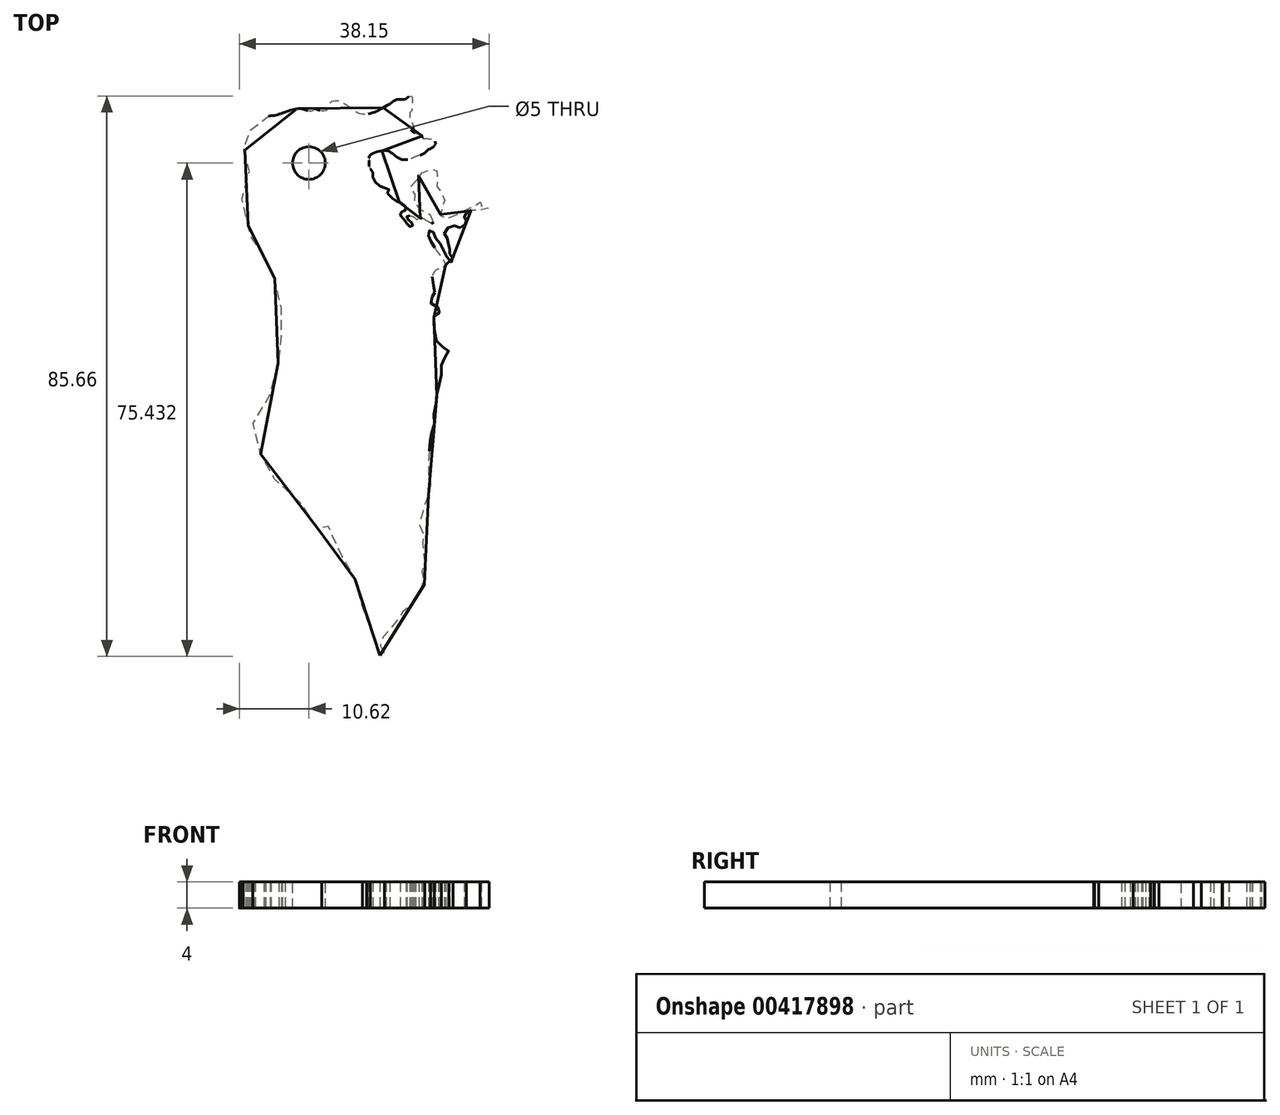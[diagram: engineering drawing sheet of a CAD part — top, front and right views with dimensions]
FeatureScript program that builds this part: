
annotation { "Feature Type Name" : "Feature", "Feature Type Description" : "" }
export const myFeature = defineFeature(function(context is Context, id is Id, definition is map)
    precondition{}
    {
        {
            var Q0;
            Q0=qCreatedBy(makeId("Top.planeOp"),FACE);
            var sketch = newSketch(context, id + "F0", { "sketchPlane" : qUnion([Q0])});
            skLineSegment(sketch, "E0", {"start": v(20.03, 43.55) * mm, "end": v(-19.97, -43.4) * mm, "construction": true});
            skFitSpline(sketch, "E1", {"points": [v(2.42, -43.12) * mm, v(2.11, -42.28) * mm, v(1.89, -41.54) * mm, v(1.61, -40.7) * mm, v(1.3, -40.08) * mm, v(1.04, -39.7) * mm, v(0.93, -39.5) * mm, v(0.91, -39.03) * mm, v(0.93, -38.74) * mm, v(0.73, -38.53) * mm, v(0.41, -38.28) * mm, v(0.36, -38.1) * mm, v(0.4, -37.63) * mm, v(0.28, -37.33) * mm, v(0.13, -37) * mm, v(-0.18, -36.47) * mm, v(-0.27, -36.24) * mm, v(-0.28, -35.8) * mm, v(-0.31, -35.3) * mm, v(-0.36, -34.97) * mm, v(-0.5, -34.42) * mm, v(-0.67, -33.87) * mm, v(-0.8, -33.2) * mm, v(-0.86, -32.8) * mm, v(-1.17, -31.97) * mm, v(-1.43, -31.38) * mm, v(-1.63, -30.87) * mm, v(-1.88, -30.12) * mm, v(-2.05, -29.75) * mm, v(-2.14, -29.6) * mm, v(-2.39, -29.27) * mm, v(-2.74, -28.88) * mm, v(-3.14, -28.42) * mm, v(-3.41, -27.95) * mm, v(-3.77, -27.3) * mm, v(-4.13, -26.63) * mm, v(-4.36, -26.2) * mm, v(-5.04, -25.12) * mm, v(-5.2, -24.78) * mm, v(-5.39, -24.19) * mm, v(-5.5, -23.5) * mm, v(-5.55, -22.95) * mm, v(-5.69, -22.62) * mm, v(-6.08, -22.41) * mm, v(-6.46, -22.55) * mm, v(-6.49, -23.01) * mm, v(-6.49, -23.44) * mm, v(-6.58, -23.83) * mm, v(-6.75, -24.07) * mm, v(-7.07, -23.82) * mm, v(-7.2, -23.36) * mm, v(-7.24, -22.88) * mm, v(-7.52, -22.31) * mm, v(-8.05, -21.84) * mm, v(-8.55, -21.3) * mm, v(-9.23, -20.48) * mm, v(-9.62, -19.95) * mm, v(-10.06, -19.32) * mm, v(-10.53, -18.74) * mm, v(-11.18, -18.08) * mm, v(-11.77, -17.56) * mm, v(-12.65, -16.91) * mm, v(-13.44, -16.4) * mm, v(-13.9, -16.01) * mm, v(-14.44, -15.45) * mm, v(-15.02, -14.82) * mm, v(-15.26, -14.49) * mm, v(-15.42, -14.17) * mm, v(-15.61, -13.44) * mm, v(-15.74, -12.78) * mm, v(-15.92, -12.14) * mm, v(-16.02, -11.93) * mm, v(-16.29, -11.06) * mm, v(-16.45, -10.33) * mm, v(-16.61, -9.76) * mm, v(-16.84, -9.2) * mm, v(-17.02, -8.71) * mm, v(-16.98, -7.69) * mm, v(-16.7, -6.99) * mm, v(-16.24, -6.2) * mm, v(-15.62, -5.4) * mm, v(-15.23, -4.84) * mm, v(-14.9, -4.34) * mm, v(-14.62, -3.74) * mm, v(-14.34, -3.16) * mm, v(-14.24, -2.1) * mm, v(-14.4, -1.23) * mm, v(-14.24, -0.16) * mm, v(-13.88, 0.64) * mm, v(-13.43, 1.26) * mm, v(-13.06, 1.74) * mm, v(-12.8, 2.24) * mm, v(-12.72, 2.67) * mm, v(-12.6, 3.16) * mm, v(-12.33, 3.65) * mm, v(-12.12, 3.96) * mm, v(-12.14, 4.84) * mm, v(-12.53, 5.37) * mm, v(-12.65, 5.9) * mm, v(-12.62, 6.4) * mm, v(-12.52, 6.73) * mm, v(-12.69, 7.34) * mm, v(-12.97, 7.9) * mm, v(-12.94, 8.76) * mm, v(-12.7, 9.05) * mm, v(-12.66, 9.65) * mm, v(-12.78, 10.5) * mm, v(-12.95, 11.26) * mm, v(-13.05, 12.08) * mm, v(-13.03, 12.7) * mm, v(-13.1, 13.25) * mm, v(-13.35, 13.89) * mm, v(-13.76, 14.67) * mm, v(-13.97, 15.18) * mm, v(-14.15, 15.64) * mm, v(-14.71, 16.15) * mm, v(-15.09, 16.48) * mm, v(-15.26, 16.78) * mm, v(-15.28, 17.21) * mm, v(-15.11, 17.47) * mm, v(-15.15, 17.78) * mm, v(-15.49, 17.98) * mm, v(-15.7, 18.33) * mm, v(-15.96, 18.93) * mm, v(-16.5, 19.5) * mm, v(-16.72, 19.76) * mm, v(-16.75, 20.11) * mm, v(-16.68, 20.52) * mm, v(-16.84, 20.83) * mm, v(-17.13, 20.97) * mm, v(-17.49, 20.9) * mm, v(-17.88, 20.59) * mm, v(-18.15, 20.52) * mm, v(-18.41, 20.79) * mm, v(-18.5, 21.09) * mm, v(-18.4, 21.52) * mm, v(-18.13, 21.87) * mm, v(-17.87, 22.17) * mm, v(-17.74, 22.4) * mm, v(-17.77, 22.64) * mm, v(-17.91, 22.98) * mm, v(-18.07, 23.3) * mm, v(-18.11, 23.9) * mm, v(-18.08, 24.38) * mm, v(-18.16, 24.68) * mm, v(-18.41, 25.18) * mm, v(-18.6, 25.82) * mm, v(-18.68, 26.32) * mm, v(-18.65, 27.05) * mm, v(-18.55, 27.74) * mm, v(-18.25, 28.54) * mm, v(-17.88, 29.17) * mm, v(-17.53, 29.77) * mm, v(-17.39, 30.17) * mm, v(-17.4, 30.64) * mm, v(-17.6, 30.96) * mm, v(-17.8, 31.33) * mm, v(-17.86, 31.7) * mm, v(-17.74, 32.15) * mm, v(-17.62, 32.45) * mm, v(-17.49, 33.08) * mm, v(-17.62, 33.5) * mm, v(-17.74, 33.7) * mm, v(-18.16, 34.06) * mm, v(-18.6, 34.43) * mm, v(-18.92, 34.84) * mm, v(-19.06, 35.41) * mm, v(-19.07, 36.03) * mm, v(-18.87, 36.58) * mm, v(-18.52, 36.9) * mm, v(-18.04, 36.92) * mm, v(-17.54, 36.92) * mm, v(-17.45, 37.2) * mm, v(-17.24, 37.48) * mm, v(-16.93, 37.75) * mm, v(-16.6, 37.98) * mm, v(-16.34, 38.29) * mm, v(-16.1, 38.64) * mm, v(-15.78, 38.99) * mm, v(-15.4, 39.23) * mm, v(-15, 39.33) * mm, v(-14.48, 39.35) * mm, v(-14.04, 39.4) * mm, v(-13.5, 39.47) * mm, v(-12.76, 39.72) * mm, v(-11.96, 39.98) * mm, v(-11.22, 40.23) * mm, v(-10.36, 40.44) * mm, v(-9.39, 40.4) * mm, v(-8.96, 40.29) * mm, v(-8.55, 40.17) * mm, v(-7.91, 40.17) * mm, v(-7.6, 40.4) * mm, v(-7.14, 40.31) * mm, v(-6.62, 40.18) * mm, v(-5.83, 40.2) * mm, v(-5.45, 40.7) * mm, v(-5.33, 41.2) * mm, v(-4.83, 41.64) * mm, v(-3.78, 41.63) * mm, v(-2.8, 41.07) * mm, v(-1.95, 40.48) * mm, v(-1.26, 40) * mm, v(-0.72, 39.75) * mm, v(-0.18, 39.64) * mm, v(0.74, 39.68) * mm, v(1.63, 39.97) * mm, v(2.41, 40.34) * mm, v(3.14, 40.73) * mm, v(4.28, 41.45) * mm, v(4.93, 41.84) * mm, v(5.64, 41.9) * mm, v(6.22, 41.9) * mm, v(6.58, 42.14) * mm, v(6.9, 42.35) * mm, v(7.3, 42.3) * mm, v(7.35, 41.53) * mm, v(7.32, 40.86) * mm, v(7.28, 40.35) * mm, v(7.24, 40.1) * mm, v(7.05, 39.94) * mm, v(6.97, 39.58) * mm, v(6.95, 39.33) * mm, v(7.07, 38.88) * mm, v(7.26, 38.44) * mm, v(7.4, 38.07) * mm, v(7.47, 37.81) * mm, v(7.45, 37.44) * mm, v(7.35, 37.26) * mm, v(7.2, 37.13) * mm, v(7.44, 36.9) * mm, v(7.9, 36.71) * mm, v(8.39, 36.6) * mm, v(8.7, 36.47) * mm, v(8.89, 36.2) * mm, v(8.88, 36.05) * mm, v(9.04, 35.88) * mm, v(9.45, 35.9) * mm, v(10, 35.84) * mm, v(10.47, 35.78) * mm, v(10.71, 35.62) * mm, v(10.88, 35.22) * mm, v(10.79, 34.87) * mm, v(10.52, 34.59) * mm, v(10.12, 34.36) * mm, v(9.76, 34.17) * mm, v(9.45, 33.89) * mm, v(9.2, 33.65) * mm, v(8.88, 33.47) * mm, v(8.42, 33.34) * mm, v(8.03, 33.2) * mm, v(7.57, 33) * mm, v(6.98, 32.76) * mm, v(6.34, 32.66) * mm, v(5.68, 32.7) * mm, v(5.06, 33.02) * mm, v(4.62, 33.36) * mm, v(4.07, 33.77) * mm, v(3.56, 34) * mm, v(2.77, 34.03) * mm, v(1.85, 33.86) * mm, v(1.12, 33.56) * mm, v(0.76, 33.21) * mm, v(0.73, 32.87) * mm, v(0.72, 32.48) * mm, v(0.73, 32.03) * mm, v(0.75, 31.6) * mm, v(1.01, 31.18) * mm, v(1.2, 30.96) * mm, v(1.3, 30.57) * mm, v(1.31, 30.15) * mm, v(1.35, 29.74) * mm, v(1.77, 29.14) * mm, v(2.2, 28.74) * mm, v(2.62, 28.44) * mm, v(3.24, 28.31) * mm, v(3.64, 28.16) * mm, v(3.9, 27.96) * mm, v(3.66, 27.7) * mm, v(3.37, 27.46) * mm, v(3.76, 27.31) * mm, v(4.05, 27.07) * mm, v(4.45, 26.65) * mm, v(4.85, 26.36) * mm, v(5.3, 26.17) * mm, v(5.84, 25.9) * mm, v(6.24, 25.57) * mm, v(6.4, 25.25) * mm, v(6.36, 25.04) * mm, v(6.07, 24.72) * mm, v(5.77, 24.69) * mm, v(5.6, 24.59) * mm, v(5.55, 24.34) * mm, v(5.55, 24.09) * mm, v(6.07, 23.52) * mm, v(6.32, 23.2) * mm, v(6.63, 22.72) * mm, v(6.81, 22.53) * mm, v(7, 22.42) * mm, v(7.23, 22.43) * mm, v(7.37, 22.55) * mm, v(7.38, 22.78) * mm, v(7.3, 22.98) * mm, v(7.08, 23.17) * mm, v(6.82, 23.38) * mm, v(6.62, 23.57) * mm, v(6.51, 23.78) * mm, v(6.52, 24) * mm, v(6.61, 24.12) * mm, v(6.96, 24.12) * mm, v(7.21, 24.03) * mm, v(7.48, 23.95) * mm, v(7.7, 23.82) * mm, v(7.94, 23.6) * mm, v(8.12, 23.53) * mm, v(8.31, 23.65) * mm, v(8.56, 23.72) * mm, v(8.95, 23.7) * mm, v(9.3, 23.52) * mm, v(9.9, 23.16) * mm, v(10.28, 22.98) * mm, v(10.5, 22.97) * mm, v(10.56, 23.1) * mm, v(10.55, 23.38) * mm, v(10.47, 23.72) * mm, v(10.36, 23.91) * mm, v(10.03, 24.26) * mm, v(9.57, 24.5) * mm, v(8.93, 24.8) * mm, v(8.49, 25.16) * mm, v(8.05, 25.62) * mm, v(7.71, 26.1) * mm, v(7.64, 26.5) * mm, v(7.78, 26.83) * mm, v(7.83, 27.15) * mm, v(7.68, 27.45) * mm, v(7.28, 27.83) * mm, v(7.08, 28.22) * mm, v(7.15, 28.75) * mm, v(7.41, 29.03) * mm, v(7.73, 29.25) * mm, v(8.02, 29.55) * mm, v(8.13, 30) * mm, v(8.4, 30.32) * mm, v(8.8, 30.64) * mm, v(9.33, 30.8) * mm, v(9.86, 31.01) * mm, v(10.33, 31.3) * mm, v(10.72, 31.46) * mm, v(10.9, 31.44) * mm, v(11.02, 31.15) * mm, v(11.18, 30.76) * mm, v(11.32, 30.48) * mm, v(11.33, 30.04) * mm, v(11.13, 29.6) * mm, v(10.91, 29.32) * mm, v(10.86, 29.03) * mm, v(11.06, 28.68) * mm, v(11.3, 28.53) * mm, v(11.55, 28.36) * mm, v(11.73, 28.07) * mm, v(11.8, 27.58) * mm, v(11.96, 27.08) * mm, v(12.13, 26.76) * mm, v(12.3, 26.45) * mm, v(12.3, 26.11) * mm, v(12.2, 25.67) * mm, v(11.94, 25.33) * mm, v(11.74, 25.03) * mm, v(11.64, 24.8) * mm, v(11.64, 24.46) * mm, v(11.66, 24.09) * mm, v(11.8, 23.88) * mm, v(12.03, 23.72) * mm, v(12.5, 23.69) * mm, v(13.01, 23.8) * mm, v(13.55, 24) * mm, v(14.25, 24.33) * mm, v(15.18, 24.79) * mm, v(16.04, 25.2) * mm, v(16.82, 25.6) * mm, v(17.48, 26.04) * mm, v(17.84, 26.17) * mm, v(17.85, 25.96) * mm, v(17.76, 25.73) * mm, v(17.75, 25.42) * mm, v(18.21, 25.44) * mm, v(18.8, 25.44) * mm, v(19.06, 25.48) * mm, v(18.99, 25.22) * mm, v(18.72, 25.03) * mm, v(18.35, 24.96) * mm, v(17.96, 24.94) * mm, v(17.58, 24.97) * mm, v(17.08, 24.99) * mm, v(16.58, 24.99) * mm, v(16.25, 24.85) * mm, v(15.86, 24.61) * mm, v(15.44, 24.36) * mm, v(15.27, 24.15) * mm, v(15.27, 23.97) * mm, v(15.46, 23.82) * mm, v(15.57, 23.64) * mm, v(15.6, 23.23) * mm, v(15.62, 22.94) * mm, v(15.52, 22.8) * mm, v(15.3, 22.68) * mm, v(14.86, 22.38) * mm, v(14.4, 22.25) * mm, v(13.97, 22.52) * mm, v(13.48, 22.55) * mm, v(12.9, 22.34) * mm, v(12.43, 21.86) * mm, v(12.22, 21.35) * mm, v(12.56, 20.98) * mm, v(12.67, 20.62) * mm, v(12.74, 20.12) * mm, v(12.88, 19.63) * mm, v(12.96, 19.33) * mm, v(13.04, 19.06) * mm, v(12.93, 18.76) * mm, v(12.94, 18.4) * mm, v(13.18, 18.14) * mm, v(13.36, 17.92) * mm, v(13.52, 17.57) * mm, v(13.55, 17.15) * mm, v(13.32, 17.01) * mm, v(12.9, 17.32) * mm, v(12.5, 17.96) * mm, v(12.18, 18.65) * mm, v(11.97, 19.2) * mm, v(11.54, 19.88) * mm, v(11.13, 20.33) * mm, v(10.83, 20.82) * mm, v(10.68, 21.28) * mm, v(10.4, 21.77) * mm, v(10.15, 21.84) * mm, v(9.97, 21.83) * mm, v(9.87, 21.63) * mm, v(9.82, 21.16) * mm, v(9.93, 20.72) * mm, v(10.14, 20.24) * mm, v(10.38, 19.84) * mm, v(10.78, 19.15) * mm, v(11.02, 18.8) * mm, v(11.6, 18.03) * mm, v(12.06, 17.37) * mm, v(12.27, 16.94) * mm, v(12.42, 16.6) * mm, v(12.43, 16.29) * mm, v(12.01, 16.32) * mm, v(11.59, 16.3) * mm, v(11.42, 16.07) * mm, v(11.14, 15.86) * mm, v(10.8, 15.64) * mm, v(10.54, 15.23) * mm, v(10.35, 14.7) * mm, v(10.35, 14) * mm, v(10.62, 13.37) * mm, v(10.74, 13.02) * mm, v(10.8, 12.58) * mm, v(10.68, 12.27) * mm, v(10.3, 12.15) * mm, v(10.36, 11.94) * mm, v(10.38, 11.68) * mm, v(10.31, 11.26) * mm, v(10.12, 11.03) * mm, v(10.3, 10.55) * mm, v(10.8, 10.29) * mm, v(11.27, 10.06) * mm, v(11.47, 9.84) * mm, v(11.55, 9.48) * mm, v(11.5, 9.28) * mm, v(11.2, 9.19) * mm, v(10.92, 9.02) * mm, v(10.7, 8.8) * mm, v(10.64, 8.47) * mm, v(10.65, 7.96) * mm, v(10.68, 7.45) * mm, v(10.74, 6.88) * mm, v(10.76, 6.41) * mm, v(10.8, 5.78) * mm, v(10.94, 5.24) * mm, v(11.16, 4.67) * mm, v(11.52, 4.38) * mm, v(12.12, 3.93) * mm, v(12.58, 3.6) * mm, v(12.82, 3.43) * mm, v(12.9, 3.37) * mm, v(12.8, 3.06) * mm, v(12.39, 2.47) * mm, v(12.07, 1.97) * mm, v(11.83, 1.48) * mm, v(11.77, 0.93) * mm, v(11.78, 0.1) * mm, v(11.74, -0.46) * mm, v(11.64, -0.92) * mm, v(11.38, -1.9) * mm, v(11.18, -2.79) * mm, v(11.1, -3.42) * mm, v(11.06, -4.12) * mm, v(10.84, -5.03) * mm, v(10.68, -5.86) * mm, v(10.67, -6.68) * mm, v(10.68, -7.66) * mm, v(10.66, -8) * mm, v(10.49, -8.62) * mm, v(10.3, -9.05) * mm, v(10.16, -9.54) * mm, v(10.08, -10.28) * mm, v(10.04, -11.05) * mm, v(9.93, -11.92) * mm, v(9.83, -12.7) * mm, v(9.84, -13.8) * mm, v(9.83, -14.83) * mm, v(9.86, -15.73) * mm, v(9.96, -16.33) * mm, v(10.13, -17) * mm, v(10.13, -17.65) * mm, v(9.8, -18.62) * mm, v(9.4, -19.45) * mm, v(9.18, -20.32) * mm, v(9.1, -20.7) * mm, v(8.8, -21.8) * mm, v(8.5, -22.44) * mm, v(8.39, -23.04) * mm, v(8.55, -23.58) * mm, v(8.9, -24.19) * mm, v(9.08, -24.7) * mm, v(9.08, -25.03) * mm, v(8.92, -25.94) * mm, v(8.83, -26.69) * mm, v(8.97, -27.24) * mm, v(9.2, -27.97) * mm, v(9.25, -28.8) * mm, v(9.04, -29.5) * mm, v(8.86, -30.16) * mm, v(8.78, -30.51) * mm, v(8.86, -31.24) * mm, v(9.12, -31.78) * mm, v(9.24, -32.19) * mm, v(8.75, -32.84) * mm, v(8.3, -33.3) * mm, v(8.03, -34) * mm, v(7.81, -34.8) * mm, v(7.36, -35.28) * mm, v(6.64, -35.7) * mm, v(6.12, -36.13) * mm, v(5.76, -36.7) * mm, v(5.29, -37.5) * mm, v(4.68, -38.22) * mm, v(4.11, -38.9) * mm, v(3.6, -39.57) * mm, v(3.24, -39.97) * mm, v(2.84, -40.37) * mm, v(2.54, -40.83) * mm, v(2.42, -41.57) * mm, v(2.7, -42.08) * mm, v(2.94, -42.6) * mm, v(3.05, -42.98) * mm, v(2.82, -43.23) * mm, v(2.53, -43.27) * mm, v(2.42, -43.12) * mm]});
            skSolve(sketch);
        }
        {
            var Q0;
            Q0=makeQuery(id+"F0.imprint","IMPRINT",FACE,{"disambiguationData":[TD([[makeQuery(id+"F0.imprint","IMPRINT",EDGE,{"derivedFrom":sQuery(id+"F0.wireOp",EDGE,"E1")}),-1.0]])]});
            extrude(context, id + "F1", {"entities" : qUnion([Q0]), "depth" : 4 * mm});
        }
        {
            var Q0;
            Q0=makeQuery(id+"F1.opExtrude","CAP_FACE",FACE,{"disambiguationData":[OSD([sQuery(id+"F0.wireOp",EDGE,"E1")])],"isStart":false});
            var sketch = newSketch(context, id + "F2", { "sketchPlane" : qUnion([Q0])});
            skCircle(sketch, "E2", {"center": v(-8.46, 32.15) * mm, "radius": 2.5 * mm});
            skSolve(sketch);
        }
        {
            var Q0;
            Q0=makeQuery(id+"F2.imprint","IMPRINT",FACE,{"disambiguationData":[TD([[makeQuery(id+"F2.imprint","IMPRINT",EDGE,{"derivedFrom":sQuery(id+"F2.wireOp",EDGE,"E2")}),1.0]])]});
            extrude(context, id + "F3", {"entities" : qUnion([Q0]), "operationType" : NewBodyOperationType.REMOVE, "oppositeDirection" : true, "depth" : 25 * mm});
        }
    });
